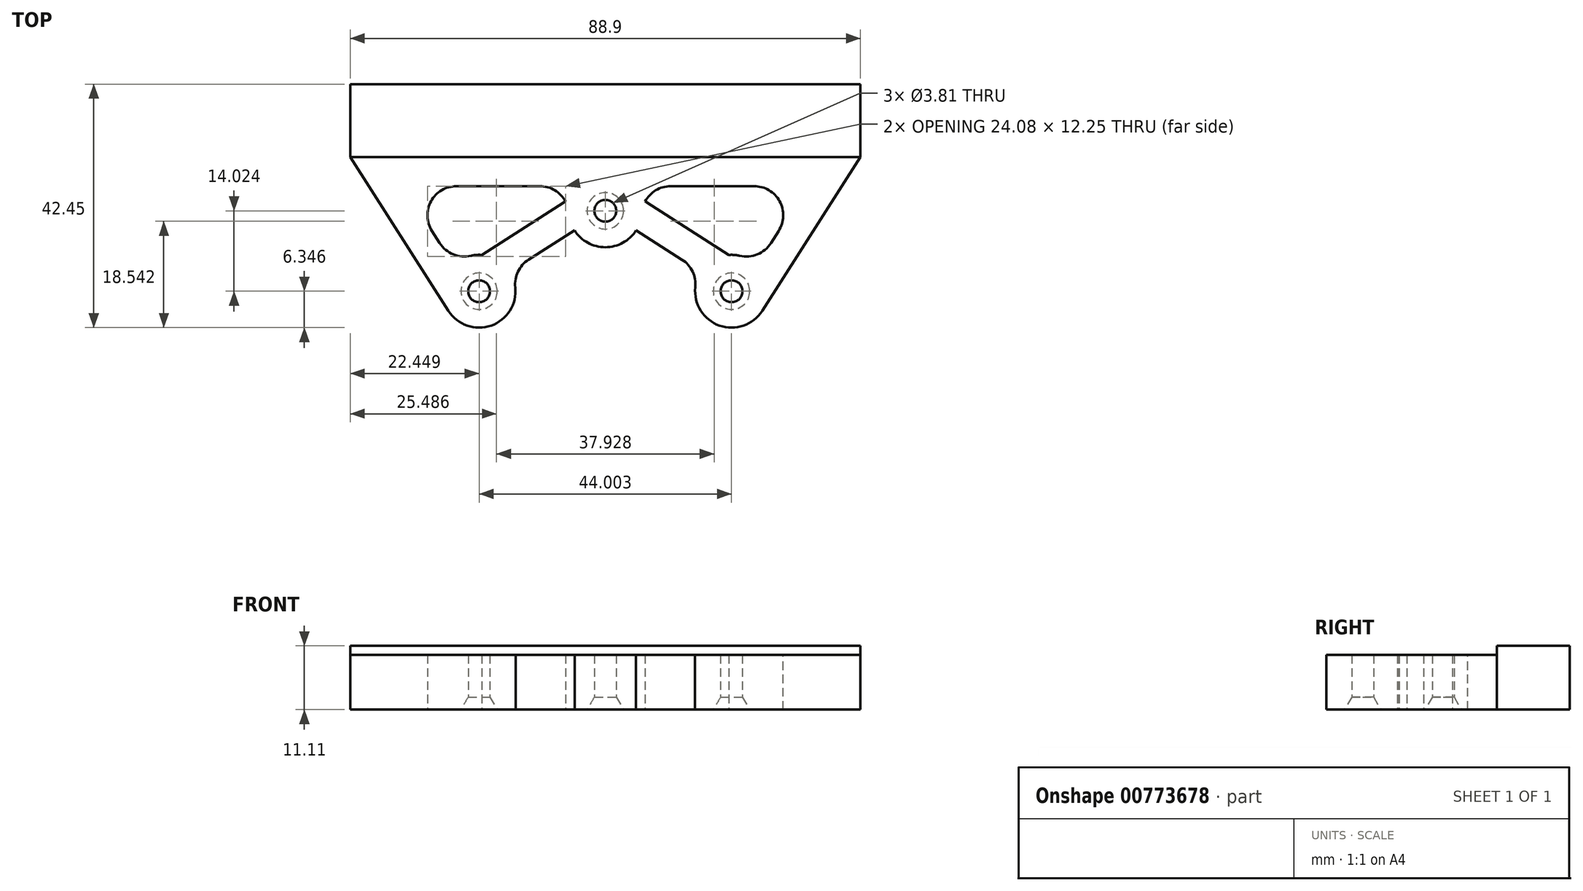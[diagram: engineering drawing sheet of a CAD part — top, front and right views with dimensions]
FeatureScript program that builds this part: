
annotation { "Feature Type Name" : "Feature", "Feature Type Description" : "" }
export const myFeature = defineFeature(function(context is Context, id is Id, definition is map)
    precondition{}
    {
        {
            var Q0;
            Q0=qCreatedBy(makeId("Top.planeOp"),FACE);
            var sketch = newSketch(context, id + "F0", { "sketchPlane" : qUnion([Q0])});
            skArc(sketch, "E0", {"start": v(-5.35, -3.41) * mm, "mid": v(0, -6.35) * mm, "end": v(5.35, -3.41) * mm});
            skArc(sketch, "E1", {"start": v(-21.52, -7.7) * mm, "mid": v(-24.16, -8.05) * mm, "end": v(-26.42, -9.46) * mm});
            skArc(sketch, "E2", {"start": v(16.65, -10.61) * mm, "mid": v(18.59, -19.38) * mm, "end": v(27.36, -17.44) * mm});
            skLineSegment(sketch, "E3", {"start": v(-22, -14.02) * mm, "end": v(0, 0) * mm, "construction": true});
            skLineSegment(sketch, "E4", {"start": v(0, 0) * mm, "end": v(22, -14.02) * mm, "construction": true});
            skLineSegment(sketch, "E5.bottom", {"start": v(-44.45, 22.08) * mm, "end": v(44.45, 22.08) * mm});
            skLineSegment(sketch, "E5.top", {"start": v(-44.45, 9.38) * mm, "end": v(44.45, 9.38) * mm, "construction": true});
            skLineSegment(sketch, "E5.left", {"start": v(-44.45, 22.08) * mm, "end": v(-44.45, 9.38) * mm});
            skLineSegment(sketch, "E5.right", {"start": v(44.45, 22.08) * mm, "end": v(44.45, 9.38) * mm});
            skPoint(sketch, "E6", {"position": v(0, 22.08) * mm});
            skLineSegment(sketch, "E7", {"start": v(-44.45, 9.38) * mm, "end": v(-27.36, -17.44) * mm});
            skLineSegment(sketch, "E8", {"start": v(44.45, 9.38) * mm, "end": v(27.36, -17.44) * mm});
            skLineSegment(sketch, "E9", {"start": v(-16.65, -10.61) * mm, "end": v(-5.35, -3.41) * mm});
            skLineSegment(sketch, "E10", {"start": v(5.35, -3.41) * mm, "end": v(16.65, -10.61) * mm});
            skLineSegment(sketch, "E11", {"start": v(-35.19, 4.3) * mm, "end": v(-4.67, 4.3) * mm});
            skLineSegment(sketch, "E12", {"start": v(-21.52, -7.7) * mm, "end": v(-5.94, 2.24) * mm});
            skLineSegment(sketch, "E13", {"start": v(-35.19, 4.3) * mm, "end": v(-26.42, -9.46) * mm});
            skLineSegment(sketch, "E14", {"start": v(-39.47, 1.57) * mm, "end": v(-35.19, 4.3) * mm, "construction": true});
            skLineSegment(sketch, "E15", {"start": v(-14.18, -9.04) * mm, "end": v(-16.91, -4.76) * mm, "construction": true});
            skLineSegment(sketch, "E16", {"start": v(-35.19, 4.3) * mm, "end": v(-35.19, 9.38) * mm, "construction": true});
            skLineSegment(sketch, "E17", {"start": v(4.67, 4.3) * mm, "end": v(35.19, 4.3) * mm});
            skLineSegment(sketch, "E18", {"start": v(35.19, 4.3) * mm, "end": v(26.42, -9.46) * mm});
            skLineSegment(sketch, "E19", {"start": v(5.94, 2.24) * mm, "end": v(21.52, -7.7) * mm});
            skArc(sketch, "E20.trimOffspring", {"start": v(5.94, 2.24) * mm, "mid": v(5.4, 3.33) * mm, "end": v(4.67, 4.3) * mm});
            skArc(sketch, "E21.trimOffspring", {"start": v(-4.67, 4.3) * mm, "mid": v(-5.4, 3.33) * mm, "end": v(-5.94, 2.24) * mm});
            skArc(sketch, "E22.trimOffspring", {"start": v(-27.36, -17.44) * mm, "mid": v(-18.59, -19.38) * mm, "end": v(-16.65, -10.61) * mm});
            skArc(sketch, "E23.trimOffspring", {"start": v(26.42, -9.46) * mm, "mid": v(24.16, -8.05) * mm, "end": v(21.52, -7.7) * mm});
            skSolve(sketch);
        }
        {
            var Q0;
            Q0 = qSketchRegion(id + "F0", true);
            extrude(context, id + "F1", {"entities" : qUnion([Q0]), "depth" : 9.52 * mm, "offsetDistance" : 25.4 * mm});
        }
        {
            var Q0;
            Q0=makeQuery(id+"F1.opExtrude","SWEPT_EDGE",EDGE,{"disambiguationData":[OSD([sQuery(id+"F0.wireOp",EDGE,"E17"),sQuery(id+"F0.wireOp",EDGE,"E18")])]});
            var Q1;
            Q1=makeQuery(id+"F1.opExtrude","SWEPT_EDGE",EDGE,{"disambiguationData":[OSD([sQuery(id+"F0.wireOp",EDGE,"E18"),sQuery(id+"F0.wireOp",EDGE,"E23.trimOffspring")])]});
            var Q2;
            Q2=makeQuery(id+"F1.opExtrude","SWEPT_EDGE",EDGE,{"disambiguationData":[OSD([sQuery(id+"F0.wireOp",EDGE,"E17"),sQuery(id+"F0.wireOp",EDGE,"E20.trimOffspring")])]});
            var Q3;
            Q3=makeQuery(id+"F1.opExtrude","SWEPT_EDGE",EDGE,{"disambiguationData":[OSD([sQuery(id+"F0.wireOp",EDGE,"E19"),sQuery(id+"F0.wireOp",EDGE,"E20.trimOffspring")])]});
            var Q4;
            Q4=makeQuery(id+"F1.opExtrude","SWEPT_EDGE",EDGE,{"disambiguationData":[OSD([sQuery(id+"F0.wireOp",EDGE,"E12"),sQuery(id+"F0.wireOp",EDGE,"E21.trimOffspring")])]});
            var Q5;
            Q5=makeQuery(id+"F1.opExtrude","SWEPT_EDGE",EDGE,{"disambiguationData":[OSD([sQuery(id+"F0.wireOp",EDGE,"E11"),sQuery(id+"F0.wireOp",EDGE,"E21.trimOffspring")])]});
            var Q6;
            Q6=makeQuery(id+"F1.opExtrude","SWEPT_EDGE",EDGE,{"disambiguationData":[OSD([sQuery(id+"F0.wireOp",EDGE,"E1"),sQuery(id+"F0.wireOp",EDGE,"E13")])]});
            var Q7;
            Q7=makeQuery(id+"F1.opExtrude","SWEPT_EDGE",EDGE,{"disambiguationData":[OSD([sQuery(id+"F0.wireOp",EDGE,"E11"),sQuery(id+"F0.wireOp",EDGE,"E13")])]});
            var Q8;
            Q8=makeQuery(id+"F1.opExtrude","SWEPT_EDGE",EDGE,{"disambiguationData":[OSD([sQuery(id+"F0.wireOp",EDGE,"E9"),sQuery(id+"F0.wireOp",EDGE,"E22.trimOffspring")])]});
            var Q9;
            Q9=makeQuery(id+"F1.opExtrude","SWEPT_EDGE",EDGE,{"disambiguationData":[OSD([sQuery(id+"F0.wireOp",EDGE,"E2"),sQuery(id+"F0.wireOp",EDGE,"E10")])]});
            fillet(context, id + "F2", {"entities" : qUnion([Q0, Q1, Q2, Q3, Q4, Q5, Q6, Q7, Q8, Q9]), "radius" : 5.08 * mm, "tangentPropagation" : true, "allowEdgeOverflow" : false});
        }
        {
            var Q0;
            Q0=makeQuery(id+"F1.opExtrude","CAP_FACE",FACE,{"disambiguationData":[OSD([sQuery(id+"F0.wireOp",EDGE,"E0"),sQuery(id+"F0.wireOp",EDGE,"E1"),sQuery(id+"F0.wireOp",EDGE,"E2"),sQuery(id+"F0.wireOp",EDGE,"E5.bottom"),sQuery(id+"F0.wireOp",EDGE,"E5.left"),sQuery(id+"F0.wireOp",EDGE,"E5.right"),sQuery(id+"F0.wireOp",EDGE,"E7"),sQuery(id+"F0.wireOp",EDGE,"E8"),sQuery(id+"F0.wireOp",EDGE,"E9"),sQuery(id+"F0.wireOp",EDGE,"E10"),sQuery(id+"F0.wireOp",EDGE,"E11"),sQuery(id+"F0.wireOp",EDGE,"E12"),sQuery(id+"F0.wireOp",EDGE,"E13"),sQuery(id+"F0.wireOp",EDGE,"E17"),sQuery(id+"F0.wireOp",EDGE,"E18"),sQuery(id+"F0.wireOp",EDGE,"E19"),sQuery(id+"F0.wireOp",EDGE,"E20.trimOffspring"),sQuery(id+"F0.wireOp",EDGE,"E21.trimOffspring"),sQuery(id+"F0.wireOp",EDGE,"E22.trimOffspring"),sQuery(id+"F0.wireOp",EDGE,"E23.trimOffspring")])],"isStart":false});
            var sketch = newSketch(context, id + "F3", { "sketchPlane" : qUnion([Q0])});
            skLineSegment(sketch, "E24.bottom", {"start": v(44.45, 22.08) * mm, "end": v(-44.45, 22.08) * mm});
            skLineSegment(sketch, "E24.top", {"start": v(44.45, 9.38) * mm, "end": v(-44.45, 9.38) * mm});
            skLineSegment(sketch, "E24.left", {"start": v(44.45, 22.08) * mm, "end": v(44.45, 9.38) * mm});
            skLineSegment(sketch, "E24.right", {"start": v(-44.45, 22.08) * mm, "end": v(-44.45, 9.38) * mm});
            skSolve(sketch);
        }
        {
            var Q0;
            Q0 = qSketchRegion(id + "F3", true);
            extrude(context, id + "F4", {"entities" : qUnion([Q0]), "operationType" : NewBodyOperationType.ADD, "depth" : 1.59 * mm, "offsetDistance" : 25.4 * mm});
        }
        {
            var Q0;
            Q0=makeQuery(id+"F1.opExtrude","CAP_FACE",FACE,{"disambiguationData":[OSD([sQuery(id+"F0.wireOp",EDGE,"E0"),sQuery(id+"F0.wireOp",EDGE,"E1"),sQuery(id+"F0.wireOp",EDGE,"E2"),sQuery(id+"F0.wireOp",EDGE,"E5.bottom"),sQuery(id+"F0.wireOp",EDGE,"E5.left"),sQuery(id+"F0.wireOp",EDGE,"E5.right"),sQuery(id+"F0.wireOp",EDGE,"E7"),sQuery(id+"F0.wireOp",EDGE,"E8"),sQuery(id+"F0.wireOp",EDGE,"E9"),sQuery(id+"F0.wireOp",EDGE,"E10"),sQuery(id+"F0.wireOp",EDGE,"E11"),sQuery(id+"F0.wireOp",EDGE,"E12"),sQuery(id+"F0.wireOp",EDGE,"E13"),sQuery(id+"F0.wireOp",EDGE,"E17"),sQuery(id+"F0.wireOp",EDGE,"E18"),sQuery(id+"F0.wireOp",EDGE,"E19"),sQuery(id+"F0.wireOp",EDGE,"E20.trimOffspring"),sQuery(id+"F0.wireOp",EDGE,"E21.trimOffspring"),sQuery(id+"F0.wireOp",EDGE,"E22.trimOffspring"),sQuery(id+"F0.wireOp",EDGE,"E23.trimOffspring")])],"isStart":true});
            var sketch = newSketch(context, id + "F5", { "sketchPlane" : qUnion([Q0])});
            skPoint(sketch, "E25", {"position": v(-22, 14.02) * mm});
            skPoint(sketch, "E26", {"position": v(0, 0) * mm});
            skPoint(sketch, "E27", {"position": v(22, 14.02) * mm});
            skSolve(sketch);
        }
        {
            var Q0;
            Q0=sQuery(id+"F5.wireOp",VERTEX,"E26");
            var Q1;
            Q1=sQuery(id+"F5.wireOp",VERTEX,"E25");
            var Q2;
            Q2=sQuery(id+"F5.wireOp",VERTEX,"E27");
            var Q3;
            Q3=makeQuery(id+"F1.opExtrude","SWEPT_BODY",BODY,{"disambiguationData":[OSD([sQuery(id+"F0.wireOp",EDGE,"E0"),sQuery(id+"F0.wireOp",EDGE,"E1"),sQuery(id+"F0.wireOp",EDGE,"E2"),sQuery(id+"F0.wireOp",EDGE,"E5.bottom"),sQuery(id+"F0.wireOp",EDGE,"E5.left"),sQuery(id+"F0.wireOp",EDGE,"E5.right"),sQuery(id+"F0.wireOp",EDGE,"E7"),sQuery(id+"F0.wireOp",EDGE,"E8"),sQuery(id+"F0.wireOp",EDGE,"E9"),sQuery(id+"F0.wireOp",EDGE,"E10"),sQuery(id+"F0.wireOp",EDGE,"E11"),sQuery(id+"F0.wireOp",EDGE,"E12"),sQuery(id+"F0.wireOp",EDGE,"E13"),sQuery(id+"F0.wireOp",EDGE,"E17"),sQuery(id+"F0.wireOp",EDGE,"E18"),sQuery(id+"F0.wireOp",EDGE,"E19"),sQuery(id+"F0.wireOp",EDGE,"E20.trimOffspring"),sQuery(id+"F0.wireOp",EDGE,"E21.trimOffspring"),sQuery(id+"F0.wireOp",EDGE,"E22.trimOffspring"),sQuery(id+"F0.wireOp",EDGE,"E23.trimOffspring")])]});
            hole(context, id + "F6", {"style" : HoleStyle.C_SINK, "endStyle" : HoleEndStyle.THROUGH, "holeDiameter" : 3.8 * mm, "cSinkDiameter" : 6.35 * mm, "cSinkAngle" : 60 * degree, "majorDiameter" : 6.35 * mm, "isTappedThrough" : true, "tappedDepth" : 12.7 * mm, "tapClearance" : 3, "startFromSketch" : true, "locations" : qUnion([Q0, Q1, Q2]), "scope" : qUnion([Q3])});
        }
    });
